# Revit family: Haworth_ComposeStorage_Open_Special
name_source: partatom
category: Furniture Systems
revit_build: Autodesk Revit 2018 (Build: 20170223_1515(x64)
units: mm (PartAtom-declared; Revit-internal decimal feet)

## family parameters
Always vertical = Yes
Cut with Voids When Loaded = No
OmniClass Number = 23.40.70.14.64.21
OmniClass Title = Systems Furniture
Part Type = Normal
Room Calculation Point = No
Round Connector Dimension = Use Diameter
Shared = No
Work Plane-Based = No

## types (4) — shared parameters
Actual Height = 22 1/4"
Assembly Code = E2020200
Base = Yes
Base Finish = Haworth _ Wood _ White Oak
Base Height = 1"
Cabinet Finish = Haworth _ Wood _ White Oak
Chamfer Legs = No
Description = Haworth - Compose Storage Open - 22High - SPECIAL
Door Finish = Haworth _ Wood _ White Oak
Drawer Height = 13"
Drawer Two Height = 8"
Manufacturer = Haworth
Max. Depth = 23"
Max. Height = 55"
Max. Width = 36"
Min. Depth = 17"
Min. Height = 19"
Min. Width = 30"
Model = BZSN
Plynth Base = No
Revision Number = 3
Side Panel Base = Yes
Size = Verify Final Dim. w/ Haworth
Spacer Finish = Haworth _ Wood _ White Oak
Spacer Height = 0"
Standard Depths = 18, 24 in.
Standard Widths = 30, 36 in.
Sustainability Info = http://media.haworth.com
Top Spacer = No
URL = www.haworth.com
URL - Product = http://www.haworth.com
Warranty = http://www.haworth.com

## per-type parameters (varying)
| type | Actual Depth | Actual Width | Custom Size | Depth | Drawer Width | Width |
| 1.5 High - 36w 24d | 23" | 36" | No | 24" | 36" | 36" |
| 1.5 High - 36w 18d | 18" | 36" | Yes | 18" | 36" | 36" |
| 1.5 High - 30w 24d | 23" | 30" | No | 24" | 30" | 30" |
| 1.5 High - 30w 18d | 18" | 30" | Yes | 18" | 30" | 30" |

## geometry (parser evidence)
native form markers: Sweep x11
no freeform markers — native parametric forms only
